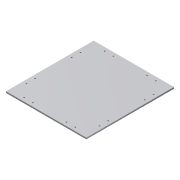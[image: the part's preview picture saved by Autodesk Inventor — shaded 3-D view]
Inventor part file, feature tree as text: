
AUTODESK INVENTOR PART (.ipt)
format: ipt  version: 2014 (Build 180170000, 170)  size: 126,976 bytes
history: native  units: mm
features: extrude x2, sketch x2, mirror x1
ambient origin geometry x8: Origin, YZ Plane, XZ Plane, XY Plane, X Axis, Y Axis, Z Axis, Center Point
bodies: Solid1 (feature_tree)
feature tree (5):
  extrude  "Extrusion1"  Depth=225.0mm
  extrude  "Extrusion2"  Depth=5.0mm
  mirror  "Mirror1"
  sketch  "Sketch1"  dims[d0=250.0mm d1=225.0mm]
  sketch  "Sketch2"  dims[d2=5.0mm d3=0.0mm d7=12.5mm d8=12.5mm d9=4.5mm d10=30.0mm d11=30.0mm d12=30.0mm d17=5.0mm d18=0.0mm d24=25.0mm d25=25.0mm d26=32.5mm d27=12.5mm d28=25.0mm d29=25.0mm]
